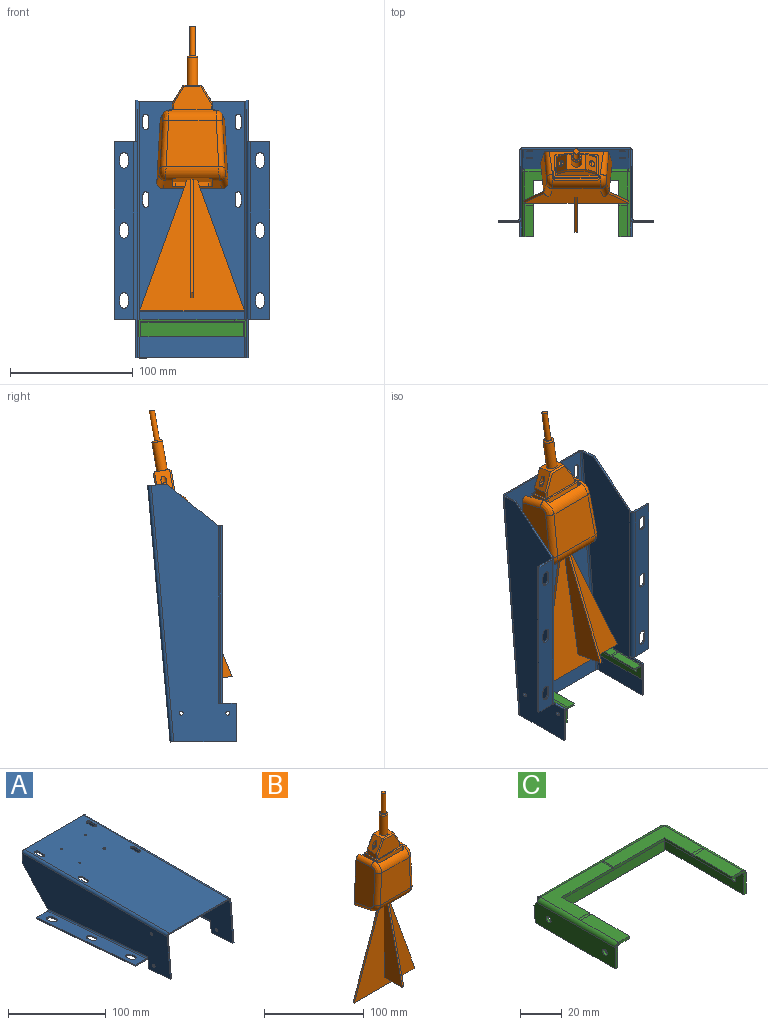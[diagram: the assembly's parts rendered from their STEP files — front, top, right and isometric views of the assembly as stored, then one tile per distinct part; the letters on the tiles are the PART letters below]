
ASSEMBLY  parts=3 mates=1
PART A: 88 faces, bbox 127x214.4x57.6 mm
  f0: plane 1.52x0.01mm, normal (0,-0.09,-1), area 0mm2, adj f13,f14,f20,f21
  f1: plane 1.52x0.14mm, normal (-1,0,0), area 0mm2, adj f21,f24,f25,f26
  f2: plane 1.52x0.01mm, normal (0,-0.09,-1), area 0mm2, adj f9,f10,f19,f28
  f3: plane 1.52x0.14mm, normal (1,0,0), area 0mm2, adj f28,f31,f32,f33
  f4: plane 91.95x15.39mm, normal (0,1,0), area 179.4mm2, adj f5,f6,f7,f8,f9,f10,f11,f12
  f5: plane 209.93x85.9mm, normal (0,0,-1), area 17788.8mm2, adj f4,f8,f12,f15,f16,f17,f18,f63
  f6: plane 209.93x85.9mm, normal (0,0,1), area 17788.8mm2, adj f4,f7,f11,f15,f16,f17,f18,f63
  f7: cylinder r=3.02mm len=209.93mm, axis (0,1,0), area 997.2mm2, adj f4,f6,f9,f81
  f8: cylinder r=1.5mm len=209.93mm, axis (0,1,0), area 494.6mm2, adj f4,f5,f10,f81
  f9: plane 214.42x53.54mm, normal (-1,0,0), area 9295.5mm2, adj f2,f4,f7,f19,f30,f61,f80,f83
  f10: plane 214.42x53.54mm, normal (1,0,0), area 9295.5mm2, adj f2,f4,f8,f19,f29,f61,f80,f83
  f11: cylinder r=3.02mm len=209.93mm, axis (0,-1,0), area 997.2mm2, adj f4,f6,f13,f81
  f12: cylinder r=1.5mm len=209.93mm, axis (0,-1,0), area 494.6mm2, adj f4,f5,f14,f81
  f13: plane 214.42x53.54mm, normal (1,0,0), area 9295.5mm2, adj f0,f4,f11,f20,f23,f62,f79,f82
  f14: plane 214.42x53.54mm, normal (-1,0,0), area 9295.5mm2, adj f0,f4,f12,f20,f22,f62,f79,f82
  f15: cylinder r=1.02mm len=2.03mm, axis (0,0,-1), area 9.7mm2, adj f5,f6
  f16: cylinder r=1.4mm len=2.79mm, axis (0,0,-1), area 13.4mm2, adj f5,f6
  f17: cylinder r=1.4mm len=2.79mm, axis (0,0,-1), area 13.4mm2, adj f5,f6
  f18: cylinder r=1.02mm len=2.03mm, axis (0,0,-1), area 9.7mm2, adj f5,f6
  f19: plane 14.55x1.52mm, normal (0,1,-0.09), area 22.3mm2, adj f2,f9,f10,f83
  f20: plane 14.55x1.52mm, normal (0,1,-0.09), area 22.3mm2, adj f0,f13,f14,f82
  f21: plane 3.02x3.01mm, normal (0,-1,0.09), area 5.4mm2, adj f0,f1,f22,f23
  f22: cylinder r=3.02mm len=144.4mm, axis (0,1,-0.09), area 687.3mm2, adj f14,f21,f25,f35
  f23: cylinder r=1.5mm len=144.27mm, axis (0,1,-0.09), area 340.9mm2, adj f13,f21,f26,f35
  f24: plane 16.03x1.52mm, normal (0,-1,0.09), area 24.4mm2, adj f1,f25,f26,f27
  f25: plane 144.15x16.03mm, normal (0,-0.09,-1), area 2095.4mm2, adj f1,f22,f24,f27,f35,f37,f38,f39
  f26: plane 144.15x16.03mm, normal (0,0.09,1), area 2095.4mm2, adj f1,f23,f24,f27,f35,f37,f38,f39
  f27: plane 144.28x14.13mm, normal (1,0,0), area 220.5mm2, adj f24,f25,f26,f35
  f28: plane 3.02x3.01mm, normal (0,-1,0.09), area 5.4mm2, adj f2,f3,f29,f30
  f29: cylinder r=3.02mm len=144.4mm, axis (0,-1,0.09), area 687.3mm2, adj f10,f28,f32,f36
  f30: cylinder r=1.5mm len=144.27mm, axis (0,-1,0.09), area 340.9mm2, adj f9,f28,f33,f36
  f31: plane 16.03x1.52mm, normal (0,-1,0.09), area 24.4mm2, adj f3,f32,f33,f34
  f32: plane 144.15x16.03mm, normal (0,-0.09,-1), area 2095.4mm2, adj f3,f29,f31,f34,f36,f49,f50,f51
  f33: plane 144.15x16.03mm, normal (0,0.09,1), area 2095.4mm2, adj f3,f30,f31,f34,f36,f49,f50,f51
  f34: plane 144.28x14.13mm, normal (-1,0,0), area 220.5mm2, adj f31,f32,f33,f36
  f35: plane 19.05x3.01mm, normal (0,1,-0.09), area 29.8mm2, adj f22,f23,f25,f26,f27,f62
  f36: plane 19.05x3.01mm, normal (0,1,-0.09), area 29.8mm2, adj f29,f30,f32,f33,f34,f61
  f37: plane 6.21x2.05mm, normal (-1,0,0), area 9.3mm2, adj f25,f26,f39,f40
  f38: plane 6.21x2.05mm, normal (1,0,0), area 9.3mm2, adj f25,f26,f39,f40
  f39: cylinder r=3.3mm len=6.6mm, axis (0,0.09,1), area 15.8mm2, adj f25,f26,f37,f38
  f40: cylinder r=3.3mm len=6.6mm, axis (0,0.09,1), area 15.8mm2, adj f25,f26,f37,f38
  f41: plane 6.21x2.05mm, normal (-1,0,0), area 9.3mm2, adj f25,f26,f43,f44
  f42: plane 6.21x2.05mm, normal (1,0,0), area 9.3mm2, adj f25,f26,f43,f44
  f43: cylinder r=3.3mm len=6.6mm, axis (0,0.09,1), area 15.8mm2, adj f25,f26,f41,f42
  f44: cylinder r=3.3mm len=6.6mm, axis (0,0.09,1), area 15.8mm2, adj f25,f26,f41,f42
  f45: plane 6.21x2.05mm, normal (-1,0,0), area 9.3mm2, adj f25,f26,f47,f48
  f46: plane 6.21x2.05mm, normal (1,0,0), area 9.3mm2, adj f25,f26,f47,f48
  f47: cylinder r=3.3mm len=6.6mm, axis (0,0.09,1), area 15.8mm2, adj f25,f26,f45,f46
  f48: cylinder r=3.3mm len=6.6mm, axis (0,0.09,1), area 15.8mm2, adj f25,f26,f45,f46
  f49: plane 6.21x2.05mm, normal (-1,0,0), area 9.3mm2, adj f32,f33,f51,f52
  f50: plane 6.21x2.05mm, normal (1,0,0), area 9.3mm2, adj f32,f33,f51,f52
  f51: cylinder r=3.3mm len=6.6mm, axis (0,0.09,1), area 15.8mm2, adj f32,f33,f49,f50
  f52: cylinder r=3.3mm len=6.6mm, axis (0,0.09,1), area 15.8mm2, adj f32,f33,f49,f50
  f53: plane 6.21x2.05mm, normal (-1,0,0), area 9.3mm2, adj f32,f33,f55,f56
  f54: plane 6.21x2.05mm, normal (1,0,0), area 9.3mm2, adj f32,f33,f55,f56
  f55: cylinder r=3.3mm len=6.6mm, axis (0,0.09,1), area 15.8mm2, adj f32,f33,f53,f54
  f56: cylinder r=3.3mm len=6.6mm, axis (0,0.09,1), area 15.8mm2, adj f32,f33,f53,f54
  f57: plane 6.21x2.05mm, normal (-1,0,0), area 9.3mm2, adj f32,f33,f59,f60
  f58: plane 6.21x2.05mm, normal (1,0,0), area 9.3mm2, adj f32,f33,f59,f60
  f59: cylinder r=3.3mm len=6.6mm, axis (0,0.09,1), area 15.8mm2, adj f32,f33,f57,f58
  f60: cylinder r=3.3mm len=6.6mm, axis (0,0.09,1), area 15.8mm2, adj f32,f33,f57,f58
  f61: plane 39.24x37.69mm, normal (0,0.72,-0.69), area 82.9mm2, adj f4,f9,f10,f36
  f62: plane 39.24x37.69mm, normal (0,0.72,-0.69), area 82.9mm2, adj f4,f13,f14,f35
  f63: cylinder r=2.41mm len=4.83mm, axis (0,0,1), area 11.6mm2, adj f5,f6,f64,f66
  f64: plane 7.87x1.52mm, normal (-1,0,0), area 12mm2, adj f5,f6,f63,f65
  f65: cylinder r=2.41mm len=4.83mm, axis (0,0,1), area 11.6mm2, adj f5,f6,f64,f66
  f66: plane 7.87x1.52mm, normal (1,0,0), area 12mm2, adj f5,f6,f63,f65
  f67: cylinder r=2.41mm len=4.83mm, axis (0,0,1), area 11.6mm2, adj f5,f6,f68,f70
  f68: plane 7.87x1.52mm, normal (-1,0,0), area 12mm2, adj f5,f6,f67,f69
  f69: cylinder r=2.41mm len=4.83mm, axis (0,0,1), area 11.6mm2, adj f5,f6,f68,f70
  f70: plane 7.87x1.52mm, normal (1,0,0), area 12mm2, adj f5,f6,f67,f69
  f71: cylinder r=2.41mm len=4.83mm, axis (0,0,1), area 11.6mm2, adj f5,f6,f72,f74
  f72: plane 7.87x1.52mm, normal (-1,0,0), area 12mm2, adj f5,f6,f71,f73
  f73: cylinder r=2.41mm len=4.83mm, axis (0,0,1), area 11.6mm2, adj f5,f6,f72,f74
  f74: plane 7.87x1.52mm, normal (1,0,0), area 12mm2, adj f5,f6,f71,f73
  f75: cylinder r=2.41mm len=4.83mm, axis (0,0,1), area 11.6mm2, adj f5,f6,f76,f78
  f76: plane 7.87x1.52mm, normal (-1,0,0), area 12mm2, adj f5,f6,f75,f77
  f77: cylinder r=2.41mm len=4.83mm, axis (0,0,1), area 11.6mm2, adj f5,f6,f76,f78
  f78: plane 7.87x1.52mm, normal (1,0,0), area 12mm2, adj f5,f6,f75,f77
  f79: plane 50.8x4.49mm, normal (0,-1,0.09), area 77.7mm2, adj f13,f14,f81,f82
  f80: plane 50.8x4.49mm, normal (0,-1,0.09), area 77.7mm2, adj f9,f10,f81,f83
  f81: plane 91.95x3.02mm, normal (0,-1,0), area 141.7mm2, adj f5,f6,f7,f8,f11,f12,f79,f80
  f82: plane 31.31x2.74mm, normal (0,-0.09,-1), area 47.9mm2, adj f13,f14,f20,f79
  f83: plane 31.31x2.74mm, normal (0,-0.09,-1), area 47.9mm2, adj f9,f10,f19,f80
  f84: cylinder r=1.64mm len=3.28mm, axis (1,0,0), area 15.7mm2, adj f13,f14
  f85: cylinder r=1.64mm len=3.28mm, axis (1,0,0), area 15.7mm2, adj f9,f10
  f86: cylinder r=1.64mm len=3.28mm, axis (1,0,0), area 15.7mm2, adj f13,f14
  f87: cylinder r=1.64mm len=3.28mm, axis (1,0,0), area 15.7mm2, adj f9,f10
PART B: 108 faces, bbox 87.3x55.6x237.3 mm
  f0: plane 6.1x6.1mm, normal (0,0,1), area 12.8mm2, adj f92,f94
  f1: plane 15.49x12.45mm, normal (0,0,1), area 134.3mm2, adj f69,f70,f83,f88,f91
  f2: cylinder r=2.16mm len=8.38mm, axis (0,0,-1), area 113.2mm2, adj f3,f6,f74,f78,f79,f80
  f3: plane 4.32x2.16mm, normal (0,0,1), area 7.3mm2, adj f2,f80
  f4: cylinder r=2.16mm len=8.38mm, axis (0,0,-1), area 113.2mm2, adj f5,f7,f73,f75,f76,f77
  f5: plane 4.3x1.96mm, normal (0,0,1), area 6.4mm2, adj f4,f77
  f6: plane 4.57x4.57mm, normal (0,0,1), area 1.8mm2, adj f2,f72
  f7: plane 4.57x4.57mm, normal (0,0,1), area 1.8mm2, adj f4,f71
  f8: plane 33.7x15.49mm, normal (0,0,1), area 27.7mm2, adj f61,f62,f63,f64,f65,f66,f67,f68
  f9: plane 44.45x24.38mm, normal (0,0,1), area 318.9mm2, adj f17,f47,f48,f49,f50,f51,f53,f54
  f10: plane 5.27x0.8mm, normal (0,0,1), area 0.9mm2, adj f21,f37,f47
  f11: plane 51.13x24.83mm, normal (0.99,-0.09,0.05), area 1223mm2, adj f17,f21,f22,f23,f33,f38
  f12: plane 51.13x24.83mm, normal (-0.99,-0.09,0.05), area 1223mm2, adj f17,f18,f19,f20,f35,f36
  f13: plane 48.26x20.57mm, normal (0,-0.14,-0.99), area 424.7mm2, adj f14,f20,f23,f24,f25,f26,f27,f31
  f14: plane 49.83x0.58mm, normal (0,0,-1), area 19.2mm2, adj f13,f17,f20,f23
  f15: plane 5.27x0.8mm, normal (0,0,1), area 0.9mm2, adj f18,f37,f51
  f16: plane 42.94x38.29mm, normal (0,-1,0), area 1567.2mm2, adj f19,f22,f34,f37
  f17: plane 61.39x58.49mm, normal (0,1,0), area 3186.9mm2, adj f9,f11,f12,f14,f18,f20,f21,f23
  f18: cylinder r=5mm len=20.26mm, axis (0.09,-1,0), area 143.2mm2, adj f12,f15,f17,f36,f51
  f19: cylinder r=5mm len=38.55mm, axis (-0.05,0,-1), area 284.4mm2, adj f12,f16,f35,f36
  f20: cylinder r=5mm len=21.24mm, axis (-0.09,0.99,-0.14), area 168.9mm2, adj f12,f13,f14,f17,f35
  f21: cylinder r=5mm len=20.26mm, axis (0.09,1,0), area 143.2mm2, adj f10,f11,f17,f38,f47
  f22: cylinder r=5mm len=38.55mm, axis (-0.05,0,1), area 284.4mm2, adj f11,f16,f33,f38
  f23: cylinder r=5mm len=21.24mm, axis (-0.09,-0.99,0.14), area 168.9mm2, adj f11,f13,f14,f17,f33
  f24: cylinder r=3mm len=3.87mm, axis (0,0,-1), area 17.2mm2, adj f13,f25,f31,f32
  f25: plane 27x3.87mm, normal (0,-1,0), area 104.4mm2, adj f13,f24,f26,f32
  f26: cylinder r=3mm len=3.87mm, axis (0,0,-1), area 17.2mm2, adj f13,f25,f27,f32
  f27: plane 14x3.45mm, normal (1,0,0), area 34.4mm2, adj f13,f26,f28,f32,f34
  f28: cylinder r=3mm len=3mm, axis (0,0,-1), area 3.1mm2, adj f27,f29,f32,f34
  f29: plane 27x0.08mm, normal (0,1,0), area 2.2mm2, adj f28,f30,f32,f34
  f30: cylinder r=3mm len=3mm, axis (0,0,-1), area 3.1mm2, adj f29,f31,f32,f34
  f31: plane 14x3.45mm, normal (-1,0,0), area 34.4mm2, adj f13,f24,f30,f32,f34
  f32: plane 33x20mm, normal (0,0,-1), area 619mm2, adj f24,f25,f26,f27,f28,f29,f30,f31
  f33: bspline ~10.84x10.27mm, area 90mm2, adj f11,f22,f23,f34
  f34: cylinder r=10mm len=44.22mm, axis (1,0,0), area 482mm2, adj f13,f16,f27,f28,f29,f30,f31,f33
  f35: bspline ~10.84x10.27mm, area 90mm2, adj f12,f19,f20,f34
  f36: bspline ~11.58x10.62mm, area 94.2mm2, adj f12,f18,f19,f37
  f37: cylinder r=10mm len=39.26mm, axis (-1,0,0), area 419.6mm2, adj f10,f15,f16,f36,f38,f47,f48,f49
  f38: bspline ~10x10mm, area 94.2mm2, adj f11,f21,f22,f37
  f39: cylinder r=1.02mm len=3.5mm, axis (0,1,0), area 22.3mm2, adj f17,f40
  f40: plane 2.03x2.03mm, normal (0,1,0), area 3.2mm2, adj f39
  f41: cylinder r=1.26mm len=3.5mm, axis (0,1,0), area 27.6mm2, adj f17,f42
  f42: plane 2.51x2.51mm, normal (0,1,0), area 5mm2, adj f41
  f43: cylinder r=1.26mm len=3.5mm, axis (0,1,0), area 27.6mm2, adj f17,f44
  f44: plane 2.51x2.51mm, normal (0,1,0), area 5mm2, adj f43
  f45: cylinder r=1.02mm len=3.5mm, axis (0,1,0), area 22.3mm2, adj f17,f46
  f46: plane 2.03x2.03mm, normal (0,1,0), area 3.2mm2, adj f45
  f47: plane 21.74x3.62mm, normal (-0.99,0.15,0), area 77.4mm2, adj f9,f10,f17,f21,f37,f48
  f48: cylinder r=3.17mm len=3.29mm, axis (0,0,1), area 12.4mm2, adj f9,f37,f47,f49
  f49: plane 31.62x2.22mm, normal (0,1,0), area 70.2mm2, adj f9,f37,f48,f50
  f50: cylinder r=3.17mm len=3.29mm, axis (0,0,1), area 12.4mm2, adj f9,f37,f49,f51
  f51: plane 21.74x3.62mm, normal (0.99,0.15,0), area 77.4mm2, adj f9,f15,f17,f18,f37,f50
  f52: plane 36.76x18.54mm, normal (0,0,1), area 156.6mm2, adj f53,f54,f55,f56,f57,f58,f59,f60
  f53: cylinder r=1.27mm len=4.32mm, axis (0,0,-1), area 8.5mm2, adj f9,f52,f54,f60
  f54: plane 16x4.32mm, normal (-1,0.03,0), area 69.1mm2, adj f9,f52,f53,f55
  f55: cylinder r=1.27mm len=4.32mm, axis (0,0,-1), area 8.8mm2, adj f9,f52,f54,f56
  f56: plane 34.22x4.32mm, normal (0,-1,0), area 147.8mm2, adj f9,f52,f55,f57
  f57: cylinder r=1.27mm len=4.32mm, axis (0,0,-1), area 8.8mm2, adj f9,f52,f56,f58
  f58: plane 16x4.32mm, normal (1,0.03,0), area 69.1mm2, adj f9,f52,f57,f59
  f59: cylinder r=1.27mm len=4.32mm, axis (0,0,-1), area 8.5mm2, adj f9,f52,f58,f60
  f60: plane 33.34x4.32mm, normal (0,1,0), area 144mm2, adj f9,f52,f53,f59
  f61: plane 15.49x4.32mm, normal (-1,-0.03,0), area 66.9mm2, adj f8,f52,f62,f64
  f62: plane 32.85x4.32mm, normal (0,-1,0), area 141.8mm2, adj f8,f52,f61,f63
  f63: plane 15.49x4.32mm, normal (1,-0.03,0), area 66.9mm2, adj f8,f52,f62,f64
  f64: plane 33.7x4.32mm, normal (0,1,0), area 145.5mm2, adj f8,f52,f61,f63
  f65: plane 12.41x10.04mm, normal (-1,0.03,0), area 121.1mm2, adj f8,f69,f84,f85,f86
  f66: plane 30.67x23.37mm, normal (0,-1,0), area 597.4mm2, adj f8,f81,f82,f83,f84,f85
  f67: plane 12.48x10.05mm, normal (1,0.03,0), area 121.7mm2, adj f8,f70,f81,f82,f89,f90
  f68: plane 29.78x23.37mm, normal (0,1,0), area 589mm2, adj f8,f86,f87,f88,f89,f90
  f69: plane 16.84x14.1mm, normal (-0.86,0,0.5), area 181.5mm2, adj f1,f65,f71,f84,f86,f87
  f70: plane 16.84x14.1mm, normal (0.86,0,0.5), area 181.5mm2, adj f1,f67,f72,f82,f89
  f71: cylinder r=2.29mm len=13.95mm, axis (0,0,1), area 141.8mm2, adj f7,f69
  f72: cylinder r=2.29mm len=13.95mm, axis (0,0,1), area 141.8mm2, adj f6,f70
  f73: plane 4.32x2.16mm, normal (0,0,1), area 7.3mm2, adj f4,f76
  f74: plane 4.3x1.96mm, normal (0,0,1), area 6.4mm2, adj f2,f79
  f75: plane 4.32x0.21mm, normal (0,0,1), area 0.9mm2, adj f4,f76,f77
  f76: plane 4.32x1.27mm, normal (1,0,0), area 5.5mm2, adj f4,f73,f75
  f77: plane 4.3x1.27mm, normal (-1,0,0), area 5.5mm2, adj f4,f5,f75
  f78: plane 4.32x0.21mm, normal (0,0,1), area 0.9mm2, adj f2,f79,f80
  f79: plane 4.3x1.27mm, normal (1,0,0), area 5.5mm2, adj f2,f74,f78
  f80: plane 4.32x1.27mm, normal (-1,0,0), area 5.5mm2, adj f2,f3,f78
  f81: plane 9.39x1.24mm, normal (0.71,-0.71,0), area 16.1mm2, adj f8,f66,f67,f82
  f82: plane 15.58x9.54mm, normal (0.61,-0.71,0.35), area 30.7mm2, adj f66,f67,f70,f81,f83
  f83: plane 15.49x1.27mm, normal (0,-0.71,0.71), area 26.5mm2, adj f1,f66,f82,f84
  f84: plane 15.64x9.54mm, normal (-0.61,-0.71,0.35), area 30.7mm2, adj f65,f66,f69,f83,f85
  f85: plane 9.46x1.27mm, normal (-0.73,-0.69,0), area 16.1mm2, adj f8,f65,f66,f84
  f86: plane 10.11x1.31mm, normal (-0.71,0.71,0), area 18.4mm2, adj f8,f65,f68,f69,f87
  f87: plane 14.87x9.16mm, normal (-0.61,0.71,0.35), area 29.2mm2, adj f68,f69,f86,f88
  f88: plane 15.49x1.27mm, normal (0,0.71,0.71), area 26.5mm2, adj f1,f68,f87,f89
  f89: plane 14.81x9.2mm, normal (0.61,0.71,0.35), area 29.2mm2, adj f67,f68,f70,f88,f90
  f90: plane 10.05x1.34mm, normal (0.69,0.73,0), area 18.3mm2, adj f8,f67,f68,f89
  f91: cylinder r=4.32mm len=23.62mm, axis (0,0,-1), area 640.9mm2, adj f1,f94
  f92: cylinder r=2.29mm len=24.89mm, axis (0,0,-1), area 357.5mm2, adj f0,f93
  f93: plane 4.57x4.57mm, normal (0,0,1), area 16.4mm2, adj f92
  f94: torus R=3.05mm, axis (0,0,1), area 48.3mm2, adj f0,f91
  f95: plane 97.41x25.99mm, normal (-1,0,0), area 1462.2mm2, adj f32,f97,f99,f107
  f96: plane 97.41x25.99mm, normal (1,0,0), area 1462.2mm2, adj f32,f97,f99,f107
  f97: plane 25.99x2mm, normal (0,0,-1), area 52mm2, adj f95,f96,f99,f107
  f98: plane 25.99x2mm, normal (0,0,-1), area 52mm2, adj f100,f101,f102,f106
  f99: plane 97.41x21.95mm, normal (0,-0.98,0.22), area 199.7mm2, adj f32,f95,f96,f97
  f100: plane 97.41x21.95mm, normal (0,0.98,0.22), area 199.7mm2, adj f32,f98,f101,f102
  f101: plane 97.41x25.99mm, normal (-1,0,0), area 1462.2mm2, adj f32,f98,f100,f106
  f102: plane 97.41x25.99mm, normal (1,0,0), area 1462.2mm2, adj f32,f98,f100,f106
  f103: plane 108.18x38.52mm, normal (0.94,0,0.34), area 229.7mm2, adj f32,f104,f106,f107
  f104: plane 85.6x2mm, normal (0,0,-1), area 171.2mm2, adj f103,f105,f106,f107
  f105: plane 108.18x38.52mm, normal (-0.94,0,0.34), area 229.7mm2, adj f32,f104,f106,f107
  f106: plane 108.18x85.6mm, normal (0,1,0), area 4898mm2, adj f32,f98,f101,f102,f103,f104,f105
  f107: plane 108.18x85.6mm, normal (0,-1,0), area 4898mm2, adj f32,f95,f96,f97,f103,f104,f105
PART C: 51 faces, bbox 88.4x55.1x14.5 mm
  f0: plane 25.67x7.24mm, normal (0,0,1), area 185.8mm2, adj f1,f6,f20,f49
  f1: plane 45.59x1.52mm, normal (-1,0,0), area 68.6mm2, adj f0,f4,f6,f7,f9,f49
  f2: plane 25.67x7.24mm, normal (0,0,1), area 185.8mm2, adj f3,f5,f28,f48
  f3: plane 45.59x1.52mm, normal (1,0,0), area 68.6mm2, adj f2,f5,f7,f8,f9,f48
  f4: plane 41.41x25.67mm, normal (0,0,1), area 433.2mm2, adj f1,f9,f12,f20,f46,f49
  f5: plane 7.24x1.52mm, normal (0,-1,0), area 11mm2, adj f2,f3,f7,f26
  f6: plane 7.24x1.52mm, normal (0,-1,0), area 11mm2, adj f0,f1,f7,f19
  f7: plane 83.82x52.83mm, normal (0,0,-1), area 1266.9mm2, adj f1,f3,f5,f6,f9,f13,f21,f29
  f8: plane 41.41x25.67mm, normal (0,0,1), area 433.2mm2, adj f3,f9,f12,f28,f46,f48
  f9: plane 69.34x1.52mm, normal (0,-1,0), area 105.3mm2, adj f1,f3,f4,f7,f8,f46
  f10: plane 2.49x2.29mm, normal (-1,0,0), area 3.9mm2, adj f12,f13,f15,f27
  f11: plane 2.49x2.29mm, normal (1,0,0), area 3.9mm2, adj f12,f13,f14,f18
  f12: cylinder r=2.29mm len=83.82mm, axis (1,0,0), area 317.7mm2, adj f4,f8,f10,f11,f16,f45
  f13: cylinder r=0.76mm len=83.82mm, axis (1,0,0), area 105.9mm2, adj f7,f10,f11,f17
  f14: plane 12.13x2.58mm, normal (1,0,0), area 18.4mm2, adj f11,f16,f17,f42
  f15: plane 12.13x2.58mm, normal (-1,0,0), area 18.4mm2, adj f10,f16,f17,f42
  f16: plane 83.82x11.99mm, normal (0,1,-0.09), area 1009.1mm2, adj f12,f14,f15,f42
  f17: plane 83.82x12.13mm, normal (0,-1,0.09), area 1020.2mm2, adj f13,f14,f15,f42
  f18: plane 2.29x2.29mm, normal (0,1,0), area 3.6mm2, adj f11,f20,f21,f39
  f19: plane 2.29x2.29mm, normal (0,-1,0), area 3.6mm2, adj f6,f20,f21,f22
  f20: cylinder r=2.29mm len=52.83mm, axis (0,-1,0), area 189.7mm2, adj f0,f4,f18,f19,f23,f50
  f21: cylinder r=0.76mm len=52.83mm, axis (0,-1,0), area 63.2mm2, adj f7,f18,f19,f24
  f22: plane 12.19x1.52mm, normal (0,-1,0), area 18.6mm2, adj f19,f23,f24,f25
  f23: plane 54.94x12.19mm, normal (1,0,0), area 646.3mm2, adj f20,f22,f25,f35,f37,f38,f39,f44
  f24: plane 54.94x12.19mm, normal (-1,0,0), area 646.3mm2, adj f21,f22,f25,f35,f37,f38,f39,f44
  f25: plane 54.06x1.52mm, normal (0,0,-1), area 82.4mm2, adj f22,f23,f24,f38
  f26: plane 2.29x2.29mm, normal (0,-1,0), area 3.6mm2, adj f5,f28,f29,f30
  f27: plane 2.29x2.29mm, normal (0,1,0), area 3.6mm2, adj f10,f28,f29,f40
  f28: cylinder r=2.29mm len=52.83mm, axis (0,1,0), area 189.7mm2, adj f2,f8,f26,f27,f31,f47
  f29: cylinder r=0.76mm len=52.83mm, axis (0,1,0), area 63.2mm2, adj f7,f26,f27,f32
  f30: plane 12.19x1.52mm, normal (0,-1,0), area 18.6mm2, adj f26,f31,f32,f33
  f31: plane 54.93x12.19mm, normal (-1,0,0), area 646.3mm2, adj f28,f30,f33,f34,f36,f40,f41,f43
  f32: plane 54.93x12.19mm, normal (1,0,0), area 646.3mm2, adj f29,f30,f33,f34,f36,f40,f41,f43
  f33: plane 54.06x1.52mm, normal (0,0,-1), area 82.4mm2, adj f30,f31,f32,f41
  f34: cylinder r=1.64mm len=3.28mm, axis (1,0,0), area 15.7mm2, adj f31,f32
  f35: cylinder r=1.64mm len=3.28mm, axis (1,0,0), area 15.7mm2, adj f23,f24
  f36: cylinder r=1.64mm len=3.28mm, axis (1,0,0), area 15.7mm2, adj f31,f32
  f37: cylinder r=1.64mm len=3.28mm, axis (1,0,0), area 15.7mm2, adj f23,f24
  f38: plane 10.09x1.52mm, normal (0,1,-0.09), area 15.4mm2, adj f23,f24,f25,f44
  f39: plane 1.52x0.01mm, normal (0,0,1), area 0mm2, adj f18,f23,f24,f44
  f40: plane 1.52x0.18mm, normal (0,0,1), area 0.3mm2, adj f27,f31,f32,f43
  f41: plane 9.91x1.52mm, normal (0,1,-0.09), area 15.2mm2, adj f31,f32,f33,f43
  f42: plane 83.82x1.53mm, normal (0,0,-1), area 128.2mm2, adj f14,f15,f16,f17
  f43: plane 2.28x1.91mm, normal (0,0.77,0.64), area 4.5mm2, adj f31,f32,f40,f41
  f44: plane 2.1x2.1mm, normal (0,0.71,0.71), area 4.5mm2, adj f23,f24,f38,f39
  f45: plane 1x0.5mm, normal (0,-1,0), area 0.4mm2, adj f12,f46
  f46: cylinder r=0.5mm len=7.24mm, axis (0,1,0), area 11.4mm2, adj f4,f8,f9,f45
  f47: plane 1.5x0.75mm, normal (1,0,0), area 0.9mm2, adj f28,f48
  f48: cylinder r=0.75mm len=7.24mm, axis (1,0,0), area 17.1mm2, adj f2,f3,f8,f47
  f49: cylinder r=0.75mm len=7.24mm, axis (-1,0,0), area 17.1mm2, adj f0,f1,f4,f50
  f50: plane 1.5x0.75mm, normal (-1,0,0), area 0.9mm2, adj f20,f49
PLACE A rot(axis=(0,0.74,0.68),180deg) t=(9.53,10.45,-7.73)mm
PLACE B rot(axis=(-1,0,0),9.7deg) t=(-63.75,13.44,108.23)mm
PLACE C rot(axis=(1,0,0),0deg) t=(-76.58,-45.59,1.52)mm
MATE revolute A.f84 <-> C.f34  axis (-1,0,0) through (9.53,-0.56,-6.63)mm
